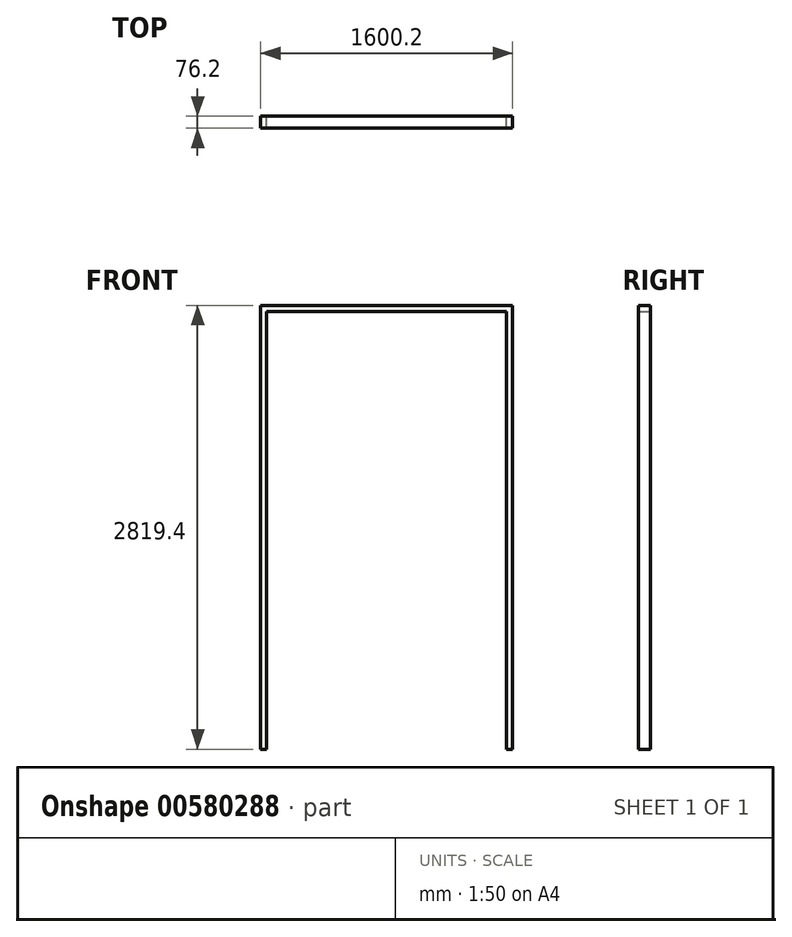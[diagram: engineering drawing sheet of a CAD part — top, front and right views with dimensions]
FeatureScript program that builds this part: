
annotation { "Feature Type Name" : "Feature", "Feature Type Description" : "" }
export const myFeature = defineFeature(function(context is Context, id is Id, definition is map)
    precondition{}
    {
        {
            var Q0;
            Q0=qCreatedBy(makeId("Front.planeOp"), FACE);
            var sketch = newSketch(context, id + "F0", { "sketchPlane" : qUnion([Q0]), "disableImprinting" : false});
            skLineSegment(sketch, "E0.top", {"start": v(0, 2781.3) * mm, "end": v(1524, 2781.3) * mm});
            skLineSegment(sketch, "E0.left", {"start": v(0, 0) * mm, "end": v(0, 2781.3) * mm});
            skLineSegment(sketch, "E0.right", {"start": v(1524, 0) * mm, "end": v(1524, 2781.3) * mm});
            skLineSegment(sketch, "E1.0", {"start": v(-38.1, 0) * mm, "end": v(-38.1, 2819.4) * mm});
            skLineSegment(sketch, "E1.1", {"start": v(-38.1, 2819.4) * mm, "end": v(1562.1, 2819.4) * mm});
            skLineSegment(sketch, "E1.2", {"start": v(1562.1, 0) * mm, "end": v(1562.1, 2819.4) * mm});
            skLineSegment(sketch, "E2", {"start": v(0, 0) * mm, "end": v(-38.1, 0) * mm});
            skLineSegment(sketch, "E3", {"start": v(1524, 0) * mm, "end": v(1562.1, 0) * mm});
            skSolve(sketch);
        }
        {
            var Q0;
            Q0 = qSketchRegion(id + "F0", true);
            extrude(context, id + "F1", {"entities" : qUnion([Q0]), "domain" : OperationDomain.MODEL, "flatOperationType" : FlatOperationType.REMOVE, "depth" : 76.2 * mm, "offsetDistance" : 25.4 * mm});
        }
    });
